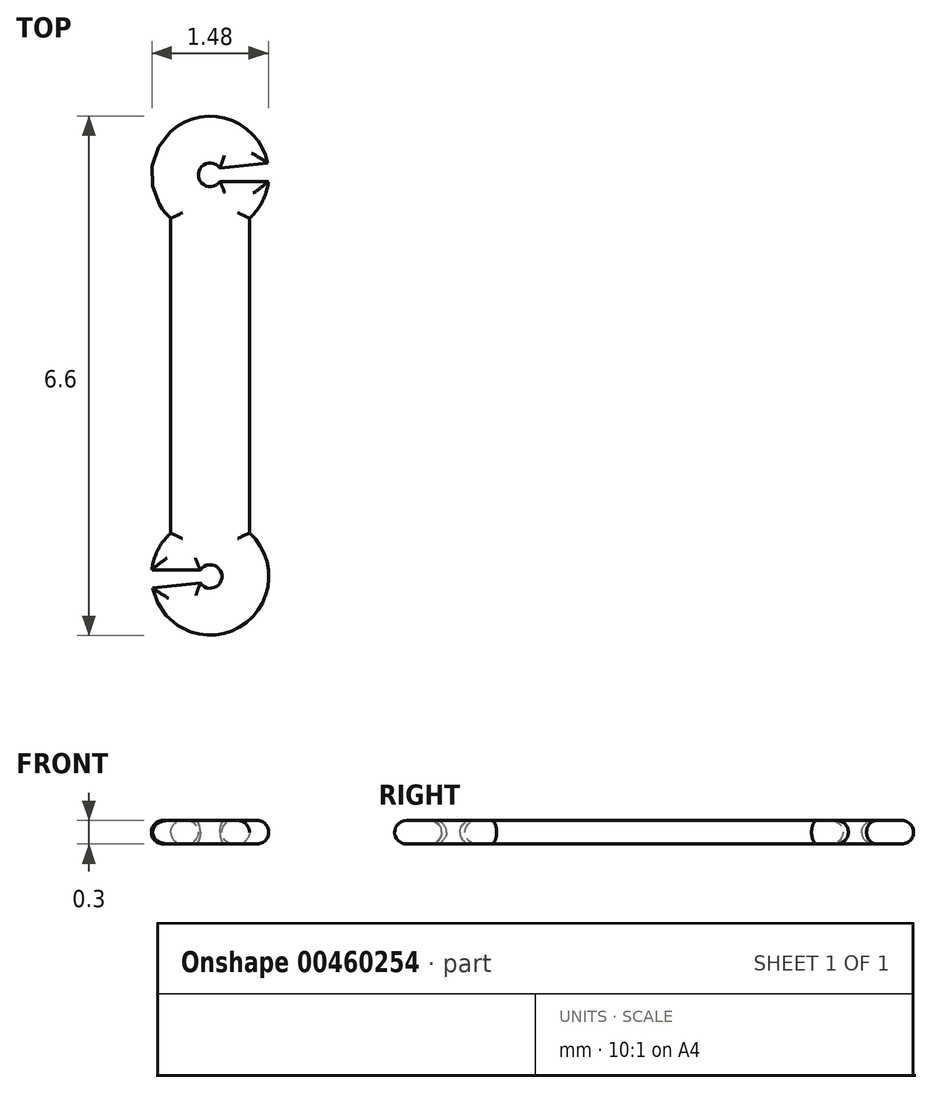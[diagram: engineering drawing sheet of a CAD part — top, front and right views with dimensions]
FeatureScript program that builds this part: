
annotation { "Feature Type Name" : "Feature", "Feature Type Description" : "" }
export const myFeature = defineFeature(function(context is Context, id is Id, definition is map)
    precondition{}
    {
        {
            var Q0;
            Q0=qCreatedBy(makeId("Top.planeOp"),FACE);
            var sketch = newSketch(context, id + "F0", { "sketchPlane" : qUnion([Q0])});
            skArc(sketch, "E0", {"start": v(0.5, 2) * mm, "mid": v(0.66, 2.21) * mm, "end": v(0.74, 2.47) * mm});
            skArc(sketch, "E1.MirrorC", {"start": v(0.5, -2) * mm, "mid": v(0.37, -3.2) * mm, "end": v(-0.73, -2.7) * mm});
            skLineSegment(sketch, "E2", {"start": v(0.5, 2) * mm, "end": v(0.5, -2) * mm});
            skLineSegment(sketch, "E3.MirrorCS", {"start": v(-0.5, 2) * mm, "end": v(-0.5, -2) * mm});
            skArc(sketch, "E4", {"start": v(0.12, 2.64) * mm, "mid": v(-0.15, 2.55) * mm, "end": v(0.12, 2.47) * mm});
            skArc(sketch, "E5.MirrorC", {"start": v(-0.12, -2.47) * mm, "mid": v(0.15, -2.55) * mm, "end": v(-0.12, -2.64) * mm});
            skLineSegment(sketch, "E6", {"start": v(0.12, 2.64) * mm, "end": v(0.73, 2.7) * mm});
            skLineSegment(sketch, "E7", {"start": v(0.12, 2.47) * mm, "end": v(0.74, 2.47) * mm});
            skLineSegment(sketch, "E8.2.0", {"start": v(-0.12, -2.47) * mm, "end": v(-0.74, -2.47) * mm});
            skLineSegment(sketch, "E8.2.1", {"start": v(-0.12, -2.64) * mm, "end": v(-0.73, -2.7) * mm});
            skPoint(sketch, "E8.center", {"position": v(0, 0) * mm});
            skArc(sketch, "E9.trimOffspring", {"start": v(0.73, 2.7) * mm, "mid": v(-0.37, 3.2) * mm, "end": v(-0.5, 2) * mm});
            skArc(sketch, "E10.trimOffspring", {"start": v(-0.74, -2.47) * mm, "mid": v(-0.66, -2.21) * mm, "end": v(-0.5, -2) * mm});
            skSolve(sketch);
        }
        {
            var Q0;
            Q0=makeQuery(id+"F0.imprint","IMPRINT",FACE,{"disambiguationData":[TD([[makeQuery(id+"F0.imprint","IMPRINT",EDGE,{"derivedFrom":sQuery(id+"F0.wireOp",EDGE,"E0")}),1.0]])]});
            extrude(context, id + "F1", {"entities" : qUnion([Q0]), "depth" : 0.3 * mm});
        }
        {
            var Q0;
            Q0=makeQuery(id+"F1.opExtrude","CAP_FACE",FACE,{"disambiguationData":[OSD([sQuery(id+"F0.wireOp",EDGE,"E0"),sQuery(id+"F0.wireOp",EDGE,"E1.MirrorC"),sQuery(id+"F0.wireOp",EDGE,"E2"),sQuery(id+"F0.wireOp",EDGE,"E3.MirrorCS"),sQuery(id+"F0.wireOp",EDGE,"E4"),sQuery(id+"F0.wireOp",EDGE,"E5.MirrorC"),sQuery(id+"F0.wireOp",EDGE,"E6"),sQuery(id+"F0.wireOp",EDGE,"E7"),sQuery(id+"F0.wireOp",EDGE,"E8.2.0"),sQuery(id+"F0.wireOp",EDGE,"E8.2.1"),sQuery(id+"F0.wireOp",EDGE,"E9.trimOffspring"),sQuery(id+"F0.wireOp",EDGE,"E10.trimOffspring")])],"isStart":false});
            fillet(context, id + "F2", {"entities" : qUnion([Q0]), "radius" : 0.15 * mm, "tangentPropagation" : true, "allowEdgeOverflow" : false});
        }
        {
            var Q0;
            {var subQ0=sQuery(id+"F0.wireOp",EDGE,"E2");Q0=makeQuery(id+"F2.opFillet","BLEND_EDGE",EDGE,{"blendedFrom":[makeQuery(id+"F1.opExtrude","CAP_EDGE",EDGE,{"disambiguationData":[OSD([subQ0])],"isStart":false}),makeQuery(id+"F1.opExtrude","SWEPT_FACE",FACE,{"disambiguationData":[OSD([subQ0])]})],"blendedInto":[makeQuery(id+"F1.opExtrude","SWEPT_FACE",FACE,{"disambiguationData":[OSD([subQ0])]})]});}
            var Q1;
            Q1=makeQuery(id+"F1.opExtrude","CAP_FACE",FACE,{"disambiguationData":[OSD([sQuery(id+"F0.wireOp",EDGE,"E0"),sQuery(id+"F0.wireOp",EDGE,"E1.MirrorC"),sQuery(id+"F0.wireOp",EDGE,"E2"),sQuery(id+"F0.wireOp",EDGE,"E3.MirrorCS"),sQuery(id+"F0.wireOp",EDGE,"E4"),sQuery(id+"F0.wireOp",EDGE,"E5.MirrorC"),sQuery(id+"F0.wireOp",EDGE,"E6"),sQuery(id+"F0.wireOp",EDGE,"E7"),sQuery(id+"F0.wireOp",EDGE,"E8.2.0"),sQuery(id+"F0.wireOp",EDGE,"E8.2.1"),sQuery(id+"F0.wireOp",EDGE,"E9.trimOffspring"),sQuery(id+"F0.wireOp",EDGE,"E10.trimOffspring")])],"isStart":true});
            fillet(context, id + "F3", {"entities" : qUnion([Q0, Q1]), "radius" : 0.15 * mm, "tangentPropagation" : true, "allowEdgeOverflow" : false});
        }
    });
